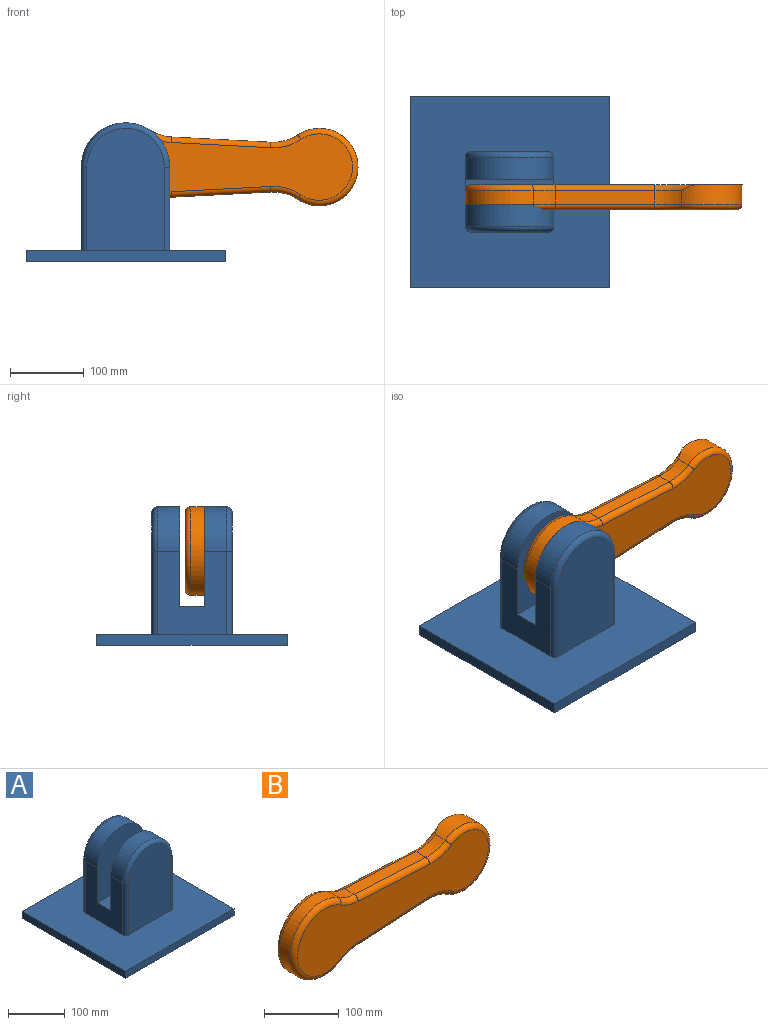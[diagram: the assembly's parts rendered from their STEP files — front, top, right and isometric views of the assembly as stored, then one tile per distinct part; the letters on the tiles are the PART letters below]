
ASSEMBLY  parts=2 mates=1
PART A: 21 faces, bbox 270x258.8x192.4 mm
  f0: plane 270x258.75mm, normal (0,0,-1), area 69862.5mm2, adj f8,f9,f10,f11
  f1: torus R=52.5mm, axis (0,-1,0), area 2119.8mm2, adj f6,f13,f14,f15
  f2: cylinder r=60mm len=120mm, axis (0,1,0), area 5654.9mm2, adj f3,f7,f12,f16
  f3: plane 135x120mm, normal (0,-1,0), area 14654.7mm2, adj f2,f4,f12,f16
  f4: plane 120x33.75mm, normal (0,0,1), area 4050mm2, adj f3,f5,f12,f16
  f5: plane 135x120mm, normal (0,1,0), area 14654.8mm2, adj f4,f6,f12,f16
  f6: cylinder r=60mm len=120mm, axis (0,1,0), area 5654.9mm2, adj f1,f5,f12,f16
  f7: torus R=52.5mm, axis (0,-1,0), area 2119.8mm2, adj f2,f17,f18,f19
  f8: plane 270x15mm, normal (0,-1,0), area 4050mm2, adj f0,f9,f11,f20
  f9: plane 258.75x15mm, normal (1,0,0), area 3881.2mm2, adj f0,f8,f10,f20
  f10: plane 270x15mm, normal (0,1,0), area 4050mm2, adj f0,f9,f11,f20
  f11: plane 258.75x15mm, normal (-1,0,0), area 3881.2mm2, adj f0,f8,f10,f20
  f12: plane 112.5x93.75mm, normal (1,0,0), area 8015.6mm2, adj f2,f3,f4,f5,f6,f13,f19,f20
  f13: cylinder r=7.5mm len=112.5mm, axis (0,0,-1), area 1325.4mm2, adj f1,f12,f14,f20
  f14: plane 165x105mm, normal (0,-1,0), area 16142mm2, adj f1,f13,f15,f20
  f15: cylinder r=7.5mm len=112.5mm, axis (0,0,-1), area 1325.4mm2, adj f1,f14,f16,f20
  f16: plane 112.5x93.75mm, normal (-1,0,0), area 8015.6mm2, adj f2,f3,f4,f5,f6,f15,f17,f20
  f17: cylinder r=7.5mm len=112.5mm, axis (0,0,-1), area 1325.4mm2, adj f7,f16,f18,f20
  f18: plane 165x105mm, normal (0,1,0), area 16142mm2, adj f7,f17,f19,f20
  f19: cylinder r=7.5mm len=112.5mm, axis (0,0,-1), area 1325.4mm2, adj f7,f12,f18,f20
  f20: plane 270x258.75mm, normal (0,0,1), area 56860.8mm2, adj f8,f9,f10,f11,f12,f13,f14,f15
PART B: 25 faces, bbox 384.2x33.8x129.8 mm
  f0: cylinder r=60mm len=29.46mm, axis (0,1,0), area 587.3mm2, adj f1,f3,f6,f9
  f1: plane 134.99x18.75mm, normal (0.05,0,-1), area 2534.5mm2, adj f0,f2,f8,f12
  f2: cylinder r=7.5mm len=135.38mm, axis (-1,0,-0.05), area 1592.5mm2, adj f1,f3,f5,f14
  f3: torus R=67.5mm, axis (0,1,0), area 385.8mm2, adj f0,f2,f4,f14
  f4: torus R=52.5mm, axis (0,1,0), area 2894.9mm2, adj f3,f6,f7,f14
  f5: torus R=67.5mm, axis (0,1,0), area 472.5mm2, adj f2,f12,f14,f15
  f6: cylinder r=60mm len=120mm, axis (0,1,0), area 4826.7mm2, adj f0,f4,f10,f16
  f7: torus R=67.5mm, axis (0,1,0), area 385.8mm2, adj f4,f14,f16,f17
  f8: cylinder r=7.5mm len=135.38mm, axis (-1,0,-0.05), area 1592.5mm2, adj f1,f9,f13,f18
  f9: torus R=67.5mm, axis (0,1,0), area 385.8mm2, adj f0,f8,f10,f18
  f10: torus R=52.5mm, axis (0,1,0), area 2894.9mm2, adj f6,f9,f11,f18
  f11: torus R=67.5mm, axis (0,1,0), area 385.8mm2, adj f10,f16,f18,f19
  f12: cylinder r=60mm len=36.37mm, axis (0,1,0), area 719.3mm2, adj f1,f5,f13,f20
  f13: torus R=67.5mm, axis (0,1,0), area 590mm2, adj f8,f12,f18,f20
  f14: plane 361.5x106.61mm, normal (0,-1,0), area 25390.2mm2, adj f2,f3,f4,f5,f7,f15,f17,f21
  f15: torus R=45mm, axis (0,1,0), area 2530.6mm2, adj f5,f14,f20,f21
  f16: cylinder r=60mm len=29.46mm, axis (0,1,0), area 587.3mm2, adj f6,f7,f11,f22
  f17: cylinder r=7.5mm len=135.38mm, axis (-1,0,0.05), area 1592.5mm2, adj f7,f14,f21,f22
  f18: plane 368.84x106.61mm, normal (0,1,0), area 26759.7mm2, adj f8,f9,f10,f11,f13,f19,f20,f23
  f19: cylinder r=7.5mm len=135.38mm, axis (-1,0,0.05), area 1592.5mm2, adj f11,f18,f22,f23
  f20: cylinder r=52.5mm len=105mm, axis (0,1,0), area 5787.9mm2, adj f12,f13,f15,f18,f23,f24
  f21: torus R=67.5mm, axis (0,1,0), area 472.5mm2, adj f14,f15,f17,f24
  f22: plane 134.99x18.75mm, normal (0.05,0,1), area 2534.5mm2, adj f16,f17,f19,f24
  f23: torus R=67.5mm, axis (0,1,0), area 590mm2, adj f18,f19,f20,f24
  f24: cylinder r=60mm len=36.37mm, axis (0,1,0), area 719.3mm2, adj f20,f21,f22,f23
PLACE A t=(-9.74,6.11,25.79)mm
PLACE B t=(-9.74,-1.39,138.29)mm
MATE revolute B.f6 <-> A.f2  axis (0,1,0) through (-9.74,-27.64,138.29)mm
